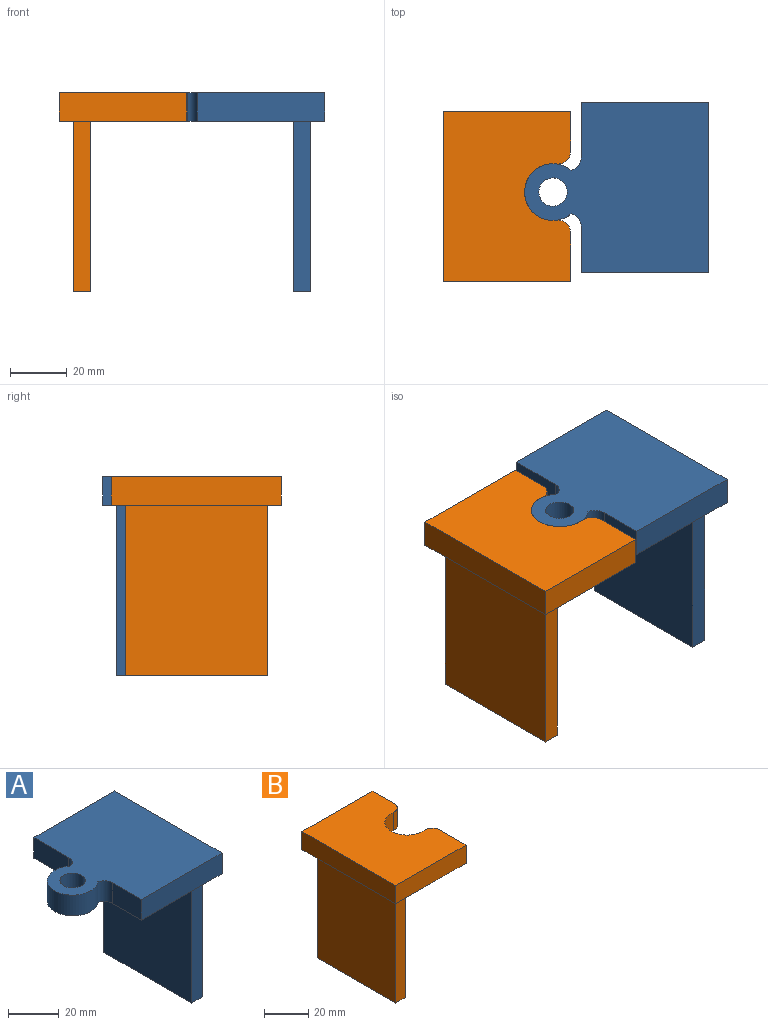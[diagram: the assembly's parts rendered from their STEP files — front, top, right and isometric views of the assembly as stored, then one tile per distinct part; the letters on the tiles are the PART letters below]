
ASSEMBLY  parts=2 mates=1
PART A: 16 faces, bbox 65x60x70 mm
  f0: plane 60x49mm, normal (-1,0,0), area 2940mm2, adj f1,f3,f4,f5
  f1: plane 60x6mm, normal (0,-1,0), area 360mm2, adj f0,f2,f4,f5
  f2: plane 60x49mm, normal (1,0,0), area 2940mm2, adj f1,f3,f4,f5
  f3: plane 60x6mm, normal (0,1,0), area 360mm2, adj f0,f2,f4,f5
  f4: plane 49x6mm, normal (0,0,-1), area 294mm2, adj f0,f1,f2,f3
  f5: plane 65x60mm, normal (0,0,-1), area 2666.8mm2, adj f0,f1,f2,f3,f6,f7,f8,f9
  f6: cylinder r=4.5mm len=10mm, axis (0,0,1), area 62mm2, adj f5,f7,f13,f15
  f7: cylinder r=10mm len=20mm, axis (0,0,1), area 452.1mm2, adj f5,f6,f8,f15
  f8: cylinder r=4.5mm len=10mm, axis (0,0,1), area 62mm2, adj f5,f7,f9,f15
  f9: plane 16.29x10mm, normal (-1,0,0), area 162.9mm2, adj f5,f8,f10,f15
  f10: plane 45x10mm, normal (0,-1,0), area 450mm2, adj f5,f9,f11,f15
  f11: plane 60x10mm, normal (1,0,0), area 600mm2, adj f5,f10,f12,f15
  f12: plane 45x10mm, normal (0,1,0), area 450mm2, adj f5,f11,f13,f15
  f13: plane 19.45x10mm, normal (-1,0,0), area 194.5mm2, adj f5,f6,f12,f15
  f14: cylinder r=5mm len=10mm, axis (0,0,1), area 314.2mm2, adj f5,f15
  f15: plane 65x60mm, normal (0,0,1), area 2960.8mm2, adj f6,f7,f8,f9,f10,f11,f12,f13
PART B: 15 faces, bbox 45x60x70 mm
  f0: plane 60x50mm, normal (-1,0,0), area 3000mm2, adj f1,f3,f4,f5
  f1: plane 60x6mm, normal (0,-1,0), area 360mm2, adj f0,f2,f4,f5
  f2: plane 60x50mm, normal (1,0,0), area 3000mm2, adj f1,f3,f4,f5
  f3: plane 60x6mm, normal (0,1,0), area 360mm2, adj f0,f2,f4,f5
  f4: plane 50x6mm, normal (0,0,-1), area 300mm2, adj f0,f1,f2,f3
  f5: plane 60x45mm, normal (0,0,-1), area 2110.4mm2, adj f0,f1,f2,f3,f6,f7,f8,f9
  f6: plane 45x10mm, normal (0,1,0), area 450mm2, adj f5,f7,f13,f14
  f7: plane 60x10mm, normal (-1,0,0), area 600mm2, adj f5,f6,f8,f14
  f8: plane 45x10mm, normal (0,-1,0), area 450mm2, adj f5,f7,f9,f14
  f9: plane 17.12x10mm, normal (1,0,0), area 171.2mm2, adj f5,f8,f10,f14
  f10: cylinder r=4.5mm len=10mm, axis (0,0,1), area 76.1mm2, adj f5,f9,f11,f14
  f11: cylinder r=10mm len=20mm, axis (0,0,1), area 338.3mm2, adj f5,f10,f12,f14
  f12: cylinder r=4.5mm len=10mm, axis (0,0,1), area 76.1mm2, adj f5,f11,f13,f14
  f13: plane 14.09x10mm, normal (1,0,0), area 140.9mm2, adj f5,f6,f12,f14
  f14: plane 60x45mm, normal (0,0,1), area 2410.4mm2, adj f6,f7,f8,f9,f10,f11,f12,f13
PLACE A t=(-8.36,-74.03,72.04)mm
PLACE B t=(31.07,-74.31,72.04)mm
MATE fastened A.f7 <-> B.f11  axis (0,0,-1) through (3.51,-74.31,62.04)mm
